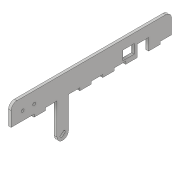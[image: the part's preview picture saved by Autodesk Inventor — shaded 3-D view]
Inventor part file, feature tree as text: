
AUTODESK INVENTOR PART (.ipt)
format: ipt  version: 2017 (Build 210142000, 142)  size: 193,024 bytes
history: native  units: in
note: dims shown in document units (in); Inventor stores cm internally (conversion verified against a paired STEP export)
features: extrude x8, sketch x8, fillet x2, projected_geometry x1
ambient origin geometry x8: Origin, YZ Plane, XZ Plane, XY Plane, X Axis, Y Axis, Z Axis, Center Point
bodies: Solid1 (feature_tree)
feature tree (19):
  extrude  "Extrusion1"  Depth=1.0in
  extrude  "Extrusion2"  Depth=0.115in TaperAngle=0.0deg
  extrude  "Extrusion3"  Depth=0.115in
  extrude  "Extrusion4"  Depth=1.0in
  fillet  "Fillet1"  Radius=0.115in
  extrude  "Extrusion5"  Depth=1.5in TaperAngle=0.0deg
  extrude  "Extrusion6"  Depth=0.25in
  fillet  "Fillet2"  Radius=0.115in
  extrude  "Extrusion7"  Depth=1.375in
  extrude  "Extrusion8"  Depth=1.0in
  sketch  "Sketch1"  dims[d0=7.0in d1=1.0in]
  sketch  "Sketch2"  dims[d2=0.0in d3=0.115in d4=0.0in]
  sketch  "Sketch3"  dims[d5=0.5in d6=0.115in]
  sketch  "Sketch4"  dims[d7=0.5in d8=2.7559in d10=1.0in d11=0.3937in d13=1.0in d15=0.115in d16=0.0in]
  projected_geometry  "Projected Loop1"
  sketch  "Sketch5"  dims[d17=1.0in d18=0.0in d19=1.5in d20=0.0in]
  sketch  "Sketch6"  dims[d21=0.25in d22=0.25in d23=0.115in]
  sketch  "Sketch7"  dims[d24=0.25in d25=1.375in]
  sketch  "Sketch9"  dims[d27=1.5in d28=0.0in d29=0.2749in d30=0.125in d31=0.125in d32=0.5in d33=0.5in d34=0.5in d35=0.5in d36=1.5in d37=0.0in d38=0.25in d39=0.5in d40=0.4in d41=1.0in d42=0.0in d43=0.125in d44=2.125in d45=0.4in d46=0.2in d47=1.0in d48=0.0in]
